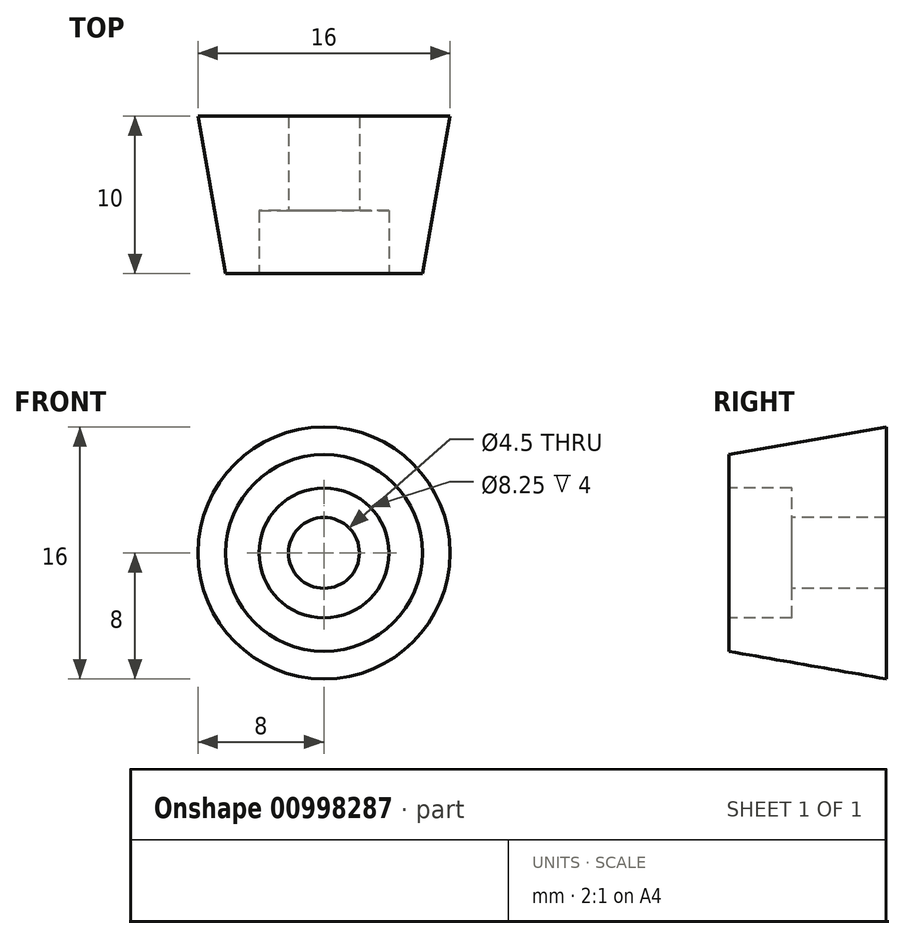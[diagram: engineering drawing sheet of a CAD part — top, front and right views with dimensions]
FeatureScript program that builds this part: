
annotation { "Feature Type Name" : "Feature", "Feature Type Description" : "" }
export const myFeature = defineFeature(function(context is Context, id is Id, definition is map)
    precondition{}
    {
        {
            var Q0;
            Q0=qCreatedBy(makeId("Front.planeOp"),FACE);
            var sketch = newSketch(context, id + "F0", { "sketchPlane" : qUnion([Q0])});
            skCircle(sketch, "E0", {"center": v(0, 0) * mm, "radius": 8 * mm});
            skSolve(sketch);
        }
        {
            var Q0;
            Q0=qCreatedBy(makeId("Front.planeOp"),FACE);
            cPlane(context, id + "F1", {"entities" : qUnion([Q0]), "cplaneType" : CPlaneType.OFFSET, "offset" : 10 * mm, "width" : 150 * mm, "height" : 150 * mm});
        }
        {
            var Q0;
            Q0=qCreatedBy(id+"F1.planeOp",FACE);
            var sketch = newSketch(context, id + "F2", { "sketchPlane" : qUnion([Q0])});
            skCircle(sketch, "E1", {"center": v(0, 0) * mm, "radius": 6.25 * mm});
            skSolve(sketch);
        }
        {
            var Q0;
            Q0=makeQuery(id+"F0.imprint","IMPRINT",FACE,{"disambiguationData":[TD([[makeQuery(id+"F0.imprint","IMPRINT",EDGE,{"derivedFrom":sQuery(id+"F0.wireOp",EDGE,"E0")}),1.0]])]});
            var Q1;
            Q1=makeQuery(id+"F2.imprint","IMPRINT",FACE,{"disambiguationData":[TD([[makeQuery(id+"F2.imprint","IMPRINT",EDGE,{"derivedFrom":sQuery(id+"F2.wireOp",EDGE,"E1")}),1.0]])]});
            loft(context, id + "F3", {"sheetProfilesArray" : [{ "sheetProfileEntities" : qUnion([Q0]) }, { "sheetProfileEntities" : qUnion([Q1]) }]});
        }
        {
            var Q0;
            Q0=makeQuery(id+"F3.opLoft","CAP_FACE",FACE,{"disambiguationData":[OSD([makeQuery(id+"F2.imprint","IMPRINT",FACE,{"disambiguationData":[TD([[makeQuery(id+"F2.imprint","IMPRINT",EDGE,{"derivedFrom":sQuery(id+"F2.wireOp",EDGE,"E1")}),1.0]])]})])],"isStart":true});
            var sketch = newSketch(context, id + "F4", { "sketchPlane" : qUnion([Q0])});
            skPoint(sketch, "E2", {"position": v(0, 0) * mm});
            skSolve(sketch);
        }
        {
            var Q0;
            Q0=sQuery(id+"F4.wireOp",VERTEX,"E2");
            var Q1;
            Q1=makeQuery(id+"F3.opLoft","SWEPT_BODY",BODY,{"disambiguationData":[OSD([makeQuery(id+"F0.imprint","IMPRINT",FACE,{"disambiguationData":[TD([[makeQuery(id+"F0.imprint","IMPRINT",EDGE,{"derivedFrom":sQuery(id+"F0.wireOp",EDGE,"E0")}),1.0]])]}),makeQuery(id+"F2.imprint","IMPRINT",FACE,{"disambiguationData":[TD([[makeQuery(id+"F2.imprint","IMPRINT",EDGE,{"derivedFrom":sQuery(id+"F2.wireOp",EDGE,"E1")}),1.0]])]})])]});
            hole(context, id + "F5", {"style" : HoleStyle.C_BORE, "endStyle" : HoleEndStyle.THROUGH, "standardTappedOrClearance" : lookupTablePath({ "fit" : "Normal", "standard" : "ISO", "size" : "M4", "type" : "Clearance" }), "standardBlindInLast" : lookupTablePath({ "fit" : "Normal", "standard" : "ISO", "engagement" : "75%", "pitch" : "0.7 mm", "size" : "M4", "type" : "Clearance & tapped" }), "holeDiameter" : 4.5 * mm, "cBoreDiameter" : 8.25 * mm, "cBoreDepth" : 4 * mm, "majorDiameter" : 4 * mm, "isTappedThrough" : true, "tappedDepth" : 12 * mm, "tapClearance" : 3, "startFromSketch" : true, "locations" : qUnion([Q0]), "scope" : qUnion([Q1])});
        }
    });
